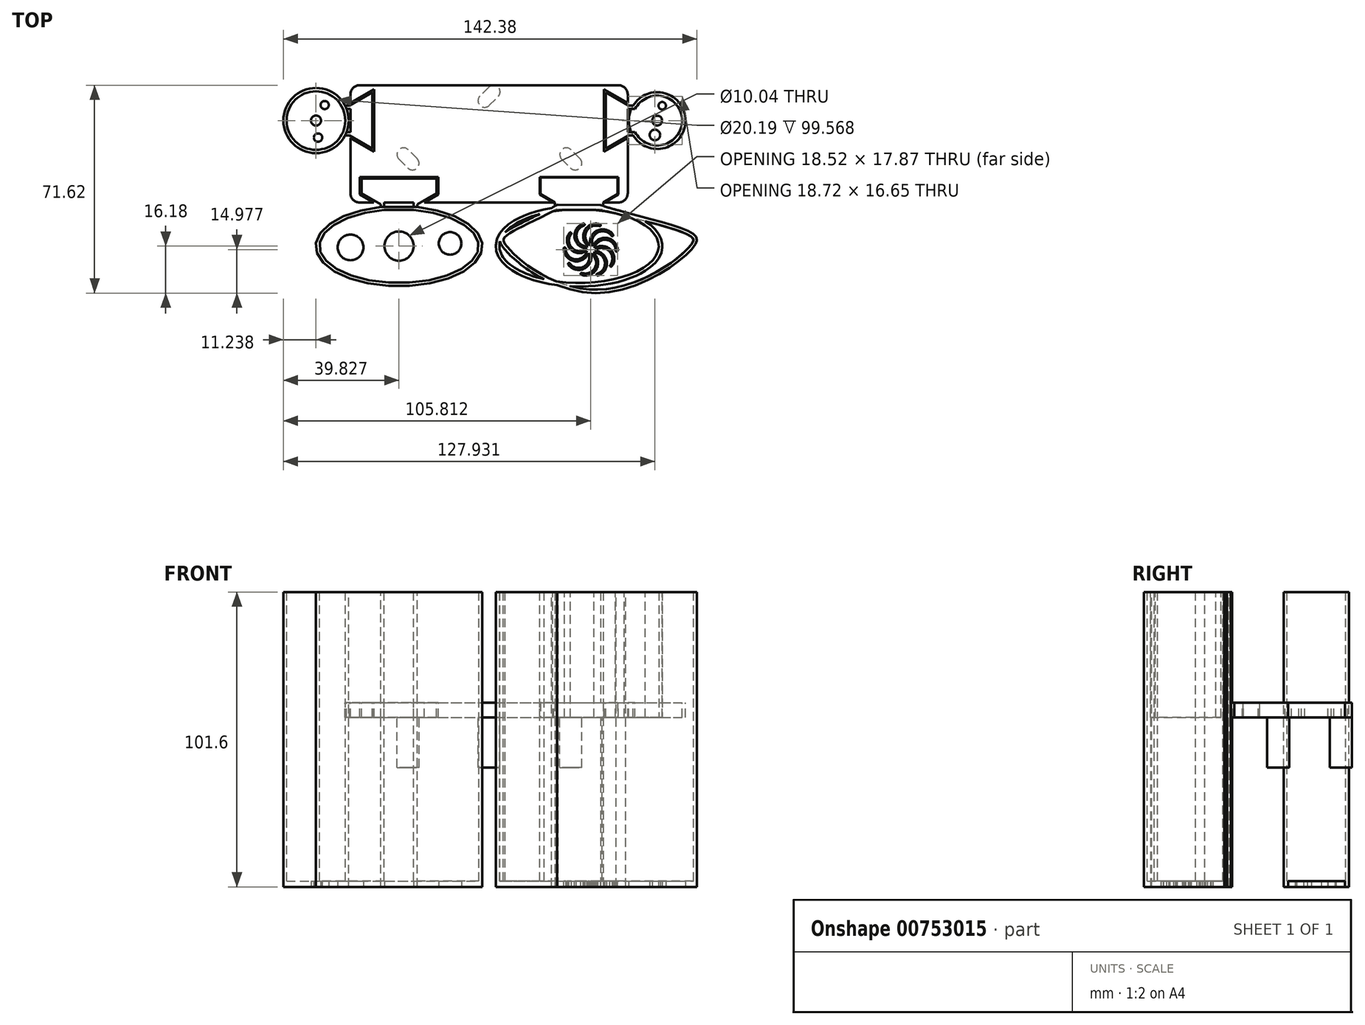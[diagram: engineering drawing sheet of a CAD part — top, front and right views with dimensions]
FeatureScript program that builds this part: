
annotation { "Feature Type Name" : "Feature", "Feature Type Description" : "" }
export const myFeature = defineFeature(function(context is Context, id is Id, definition is map)
    precondition{}
    {
        {
            var Q0;
            Q0=qCreatedBy(makeId("Top.planeOp"),FACE);
            var sketch = newSketch(context, id + "F0", { "sketchPlane" : qUnion([Q0])});
            skLineSegment(sketch, "E0.bottom", {"start": v(-47.75, 97.16) * mm, "end": v(47.75, 97.16) * mm, "construction": true});
            skLineSegment(sketch, "E0.top", {"start": v(-44.58, 0) * mm, "end": v(44.58, 0) * mm});
            skLineSegment(sketch, "E0.left", {"start": v(-47.75, 37.25) * mm, "end": v(-47.75, 3.17) * mm});
            skLineSegment(sketch, "E0.right", {"start": v(47.75, 37.25) * mm, "end": v(47.75, 3.18) * mm});
            skLineSegment(sketch, "E1", {"start": v(25.02, 14.93) * mm, "end": v(28.07, 11.88) * mm});
            skArc(sketch, "E2", {"start": v(28.07, 11.88) * mm, "mid": v(31.3, 11.88) * mm, "end": v(31.3, 15.11) * mm});
            skLineSegment(sketch, "E3", {"start": v(31.3, 15.11) * mm, "end": v(28.25, 18.16) * mm});
            skArc(sketch, "E4", {"start": v(28.25, 18.16) * mm, "mid": v(25.02, 18.16) * mm, "end": v(25.02, 14.93) * mm});
            skLineSegment(sketch, "E5", {"start": v(23, 15.51) * mm, "end": v(28.65, 9.86) * mm, "construction": true});
            skArc(sketch, "E6", {"start": v(28.65, 9.86) * mm, "mid": v(33.32, 9.86) * mm, "end": v(33.32, 14.53) * mm, "construction": true});
            skLineSegment(sketch, "E7", {"start": v(33.32, 14.53) * mm, "end": v(27.67, 20.18) * mm, "construction": true});
            skArc(sketch, "E8", {"start": v(27.67, 20.18) * mm, "mid": v(23, 20.18) * mm, "end": v(23, 15.51) * mm, "construction": true});
            skLineSegment(sketch, "E9", {"start": v(-31.04, 14.93) * mm, "end": v(-27.99, 11.88) * mm});
            skArc(sketch, "E10", {"start": v(-27.99, 11.88) * mm, "mid": v(-24.76, 11.88) * mm, "end": v(-24.76, 15.11) * mm});
            skLineSegment(sketch, "E11", {"start": v(-24.76, 15.11) * mm, "end": v(-27.8, 18.16) * mm});
            skArc(sketch, "E12", {"start": v(-27.8, 18.16) * mm, "mid": v(-31.04, 18.16) * mm, "end": v(-31.04, 14.93) * mm});
            skLineSegment(sketch, "E13", {"start": v(0.09, 33.47) * mm, "end": v(3.14, 36.52) * mm});
            skArc(sketch, "E14", {"start": v(3.14, 36.52) * mm, "mid": v(3.14, 39.75) * mm, "end": v(-0.09, 39.75) * mm});
            skLineSegment(sketch, "E15", {"start": v(-0.09, 39.75) * mm, "end": v(-3.14, 36.7) * mm});
            skArc(sketch, "E16", {"start": v(-3.14, 36.7) * mm, "mid": v(-3.14, 33.47) * mm, "end": v(0.09, 33.47) * mm});
            skLineSegment(sketch, "E17", {"start": v(25.33, 17.85) * mm, "end": v(30.99, 12.2) * mm, "construction": true});
            skLineSegment(sketch, "E18", {"start": v(26.63, 16.55) * mm, "end": v(29.69, 13.5) * mm, "construction": true});
            skPoint(sketch, "E19", {"position": v(28.16, 15.02) * mm});
            skLineSegment(sketch, "E20", {"start": v(-1.53, 35.08) * mm, "end": v(1.53, 38.14) * mm, "construction": true});
            skLineSegment(sketch, "E21", {"start": v(-29.43, 16.55) * mm, "end": v(-26.37, 13.5) * mm, "construction": true});
            skPoint(sketch, "E22", {"position": v(0, 36.61) * mm});
            skLineSegment(sketch, "E23", {"start": v(26.48, 8.9) * mm, "end": v(34.3, 8.89) * mm, "construction": true});
            skLineSegment(sketch, "E24", {"start": v(34.3, 8.89) * mm, "end": v(34.3, 17.52) * mm, "construction": true});
            skLineSegment(sketch, "E25", {"start": v(-44.58, 40.42) * mm, "end": v(44.58, 40.42) * mm});
            skPoint(sketch, "E26.visualSharp", {"position": v(-47.75, 0) * mm});
            skArc(sketch, "E26.filletArc", {"start": v(-47.75, 3.17) * mm, "mid": v(-46.82, 0.93) * mm, "end": v(-44.58, 0) * mm});
            skPoint(sketch, "E27.visualSharp", {"position": v(47.75, 0) * mm});
            skArc(sketch, "E27.filletArc", {"start": v(44.58, 0) * mm, "mid": v(46.82, 0.93) * mm, "end": v(47.75, 3.18) * mm});
            skArc(sketch, "E28.filletArc", {"start": v(47.75, 37.25) * mm, "mid": v(46.82, 39.5) * mm, "end": v(44.58, 40.42) * mm});
            skArc(sketch, "E29.filletArc", {"start": v(-44.58, 40.42) * mm, "mid": v(-46.82, 39.5) * mm, "end": v(-47.75, 37.25) * mm});
            skSolve(sketch);
        }
        {
            var Q0;
            Q0=makeQuery(id+"F0.imprint","IMPRINT",FACE,{"disambiguationData":[TD([[makeQuery(id+"F0.imprint","IMPRINT",EDGE,{"derivedFrom":sQuery(id+"F0.wireOp",EDGE,"E0.top")}),1.0]])]});
            var Q1;
            Q1=makeQuery(id+"F0.imprint","IMPRINT",FACE,{"disambiguationData":[TD([[makeQuery(id+"F0.imprint","IMPRINT",EDGE,{"derivedFrom":sQuery(id+"F0.wireOp",EDGE,"E9")}),1.0]])]});
            var Q2;
            {var subQ3=sQuery(id+"F0.wireOp",EDGE,"E13");Q2=makeQuery(id+"F0.imprint","IMPRINT",FACE,{"disambiguationData":[TD([[makeQuery(id+"F0.imprint","IMPRINT",EDGE,{"derivedFrom":subQ3}),1.0]])]});}
            var Q3;
            Q3=makeQuery(id+"F0.imprint","IMPRINT",FACE,{"disambiguationData":[TD([[makeQuery(id+"F0.imprint","IMPRINT",EDGE,{"derivedFrom":sQuery(id+"F0.wireOp",EDGE,"E1")}),1.0]])]});
            extrude(context, id + "F1", {"entities" : qUnion([Q0, Q1, Q2, Q3]), "depth" : 5.08 * mm, "offsetDistance" : 25.4 * mm});
        }
        {
            var Q0;
            Q0=makeQuery(id+"F0.imprint","IMPRINT",FACE,{"disambiguationData":[TD([[makeQuery(id+"F0.imprint","IMPRINT",EDGE,{"derivedFrom":sQuery(id+"F0.wireOp",EDGE,"E1")}),1.0]])]});
            var Q1;
            {var subQ3=sQuery(id+"F0.wireOp",EDGE,"E13");Q1=makeQuery(id+"F0.imprint","IMPRINT",FACE,{"disambiguationData":[TD([[makeQuery(id+"F0.imprint","IMPRINT",EDGE,{"derivedFrom":subQ3}),1.0]])]});}
            var Q2;
            Q2=makeQuery(id+"F0.imprint","IMPRINT",FACE,{"disambiguationData":[TD([[makeQuery(id+"F0.imprint","IMPRINT",EDGE,{"derivedFrom":sQuery(id+"F0.wireOp",EDGE,"E9")}),1.0]])]});
            var Q3;
            Q3=sQuery(id+"F0.wireOp",EDGE,"E2");
            var Q4;
            Q4=sQuery(id+"F0.wireOp",EDGE,"E3");
            var Q5;
            Q5=sQuery(id+"F0.wireOp",EDGE,"E4");
            var Q6;
            Q6=sQuery(id+"F0.wireOp",EDGE,"E1");
            extrude(context, id + "F2", {"entities" : qUnion([Q0, Q1, Q2]), "operationType" : NewBodyOperationType.ADD, "surfaceEntities" : qUnion([Q3, Q4, Q5, Q6]), "oppositeDirection" : true, "depth" : 17.27 * mm, "offsetDistance" : 25.4 * mm});
        }
        {
            var Q0;
            Q0=makeQuery(id+"F1.opExtrude","CAP_FACE",FACE,{"disambiguationData":[OSD([sQuery(id+"F0.wireOp",EDGE,"E0.top"),sQuery(id+"F0.wireOp",EDGE,"E0.left"),sQuery(id+"F0.wireOp",EDGE,"E0.right"),sQuery(id+"F0.wireOp",EDGE,"E25"),sQuery(id+"F0.wireOp",EDGE,"E26.filletArc"),sQuery(id+"F0.wireOp",EDGE,"E27.filletArc"),sQuery(id+"F0.wireOp",EDGE,"E28.filletArc"),sQuery(id+"F0.wireOp",EDGE,"E29.filletArc")])],"isStart":false});
            var sketch = newSketch(context, id + "F3", { "sketchPlane" : qUnion([Q0])});
            skLineSegment(sketch, "E30", {"start": v(47.75, 32.19) * mm, "end": v(41.4, 35.85) * mm});
            skLineSegment(sketch, "E31", {"start": v(41.4, 35.85) * mm, "end": v(41.4, 20.61) * mm});
            skLineSegment(sketch, "E32", {"start": v(41.4, 20.61) * mm, "end": v(47.75, 24.28) * mm});
            skLineSegment(sketch, "E33", {"start": v(47.75, 32.19) * mm, "end": v(47.75, 24.28) * mm});
            skLineSegment(sketch, "E34", {"start": v(47.75, 32.19) * mm, "end": v(50.3, 32.19) * mm});
            skArc(sketch, "E35", {"start": v(50.3, 24.28) * mm, "mid": v(66.47, 28.23) * mm, "end": v(50.3, 32.19) * mm});
            skLineSegment(sketch, "E36", {"start": v(50.3, 24.28) * mm, "end": v(47.75, 24.28) * mm});
            skLineSegment(sketch, "E37", {"start": v(41.4, 28.23) * mm, "end": v(57.9, 28.23) * mm, "construction": true});
            skLineSegment(sketch, "E38", {"start": v(50.3, 32.19) * mm, "end": v(50.3, 24.28) * mm, "construction": true});
            skPoint(sketch, "E39.positionSnap0", {"position": v(50.3, 28.23) * mm});
            skEllipticalArc(sketch, "E40", {});
            skLineSegment(sketch, "E41", {"start": v(31, -15.02) * mm, "end": v(58.42, -15.02) * mm, "construction": true});
            skLineSegment(sketch, "E42", {"start": v(25.91, 0) * mm, "end": v(19.31, 3.8) * mm});
            skLineSegment(sketch, "E43", {"start": v(19.31, 3.81) * mm, "end": v(19.31, 6.99) * mm});
            skLineSegment(sketch, "E44", {"start": v(19.31, 6.99) * mm, "end": v(42.67, 6.99) * mm});
            skLineSegment(sketch, "E45", {"start": v(42.67, 6.99) * mm, "end": v(42.67, 3.81) * mm});
            skLineSegment(sketch, "E46", {"start": v(42.67, 3.8) * mm, "end": v(36.07, 0) * mm});
            skLineSegment(sketch, "E47", {"start": v(36.07, 0) * mm, "end": v(25.91, 0) * mm});
            skLineSegment(sketch, "E48", {"start": v(31, 0) * mm, "end": v(31, 6.99) * mm, "construction": true});
            skLineSegment(sketch, "E49", {"start": v(25.91, 0) * mm, "end": v(25.91, -2.54) * mm});
            skLineSegment(sketch, "E50", {"start": v(36.07, 0) * mm, "end": v(36.07, -2.54) * mm});
            skFitSpline(sketch, "E51.0", {"points": [v(59.52, -16.54) * mm, v(59.68, -15.02) * mm, v(59.52, -13.5) * mm, v(59.04, -12.04) * mm, v(58.29, -10.65) * mm, v(57.27, -9.35) * mm, v(56.02, -8.12) * mm, v(54.54, -6.97) * mm, v(53.12, -6.09) * mm, v(51.88, -5.42) * mm, v(50.9, -4.95) * mm, v(49.87, -4.5) * mm, v(48.45, -3.93) * mm, v(46.59, -3.29) * mm, v(44.22, -2.63) * mm, v(41.73, -2.09) * mm, v(39.15, -1.66) * mm, v(36.5, -1.35) * mm, v(34.22, -1.2) * mm, v(32.38, -1.13) * mm, v(31, -1.12) * mm, v(29.6, -1.13) * mm, v(27.77, -1.2) * mm, v(25.5, -1.35) * mm, v(22.83, -1.66) * mm, v(20.25, -2.09) * mm, v(17.77, -2.63) * mm, v(15.4, -3.29) * mm, v(13.53, -3.93) * mm, v(12.11, -4.5) * mm, v(11.08, -4.95) * mm, v(10.1, -5.42) * mm, v(8.86, -6.09) * mm, v(7.45, -6.97) * mm, v(5.97, -8.12) * mm, v(4.71, -9.35) * mm, v(3.7, -10.65) * mm, v(2.94, -12.04) * mm, v(2.47, -13.5) * mm, v(2.3, -15.02) * mm, v(2.47, -16.54) * mm, v(2.94, -18) * mm, v(3.7, -19.39) * mm, v(4.71, -20.7) * mm, v(5.97, -21.92) * mm, v(7.45, -23.07) * mm, v(8.86, -23.95) * mm, v(10.1, -24.62) * mm, v(11.08, -25.1) * mm, v(12.11, -25.55) * mm, v(13.53, -26.11) * mm, v(15.4, -26.75) * mm, v(17.77, -27.4) * mm, v(20.25, -27.95) * mm, v(22.83, -28.38) * mm, v(25.5, -28.69) * mm, v(27.77, -28.85) * mm, v(29.6, -28.9) * mm, v(31, -28.93) * mm, v(32.38, -28.9) * mm, v(34.22, -28.85) * mm, v(36.5, -28.69) * mm, v(39.15, -28.38) * mm, v(41.73, -27.95) * mm, v(44.22, -27.4) * mm, v(46.59, -26.75) * mm, v(48.45, -26.11) * mm, v(49.87, -25.55) * mm, v(50.9, -25.1) * mm, v(51.88, -24.62) * mm, v(53.12, -23.95) * mm, v(54.54, -23.07) * mm, v(56.02, -21.92) * mm, v(57.27, -20.7) * mm, v(58.29, -19.39) * mm, v(59.04, -18) * mm, v(59.52, -16.54) * mm, v(59.68, -15.02) * mm, v(59.52, -13.5) * mm]});
            skLineSegment(sketch, "E51.1", {"start": v(18.11, 3.12) * mm, "end": v(18.11, 8.19) * mm});
            skLineSegment(sketch, "E51.2", {"start": v(18.11, 8.19) * mm, "end": v(43.87, 8.19) * mm});
            skLineSegment(sketch, "E51.3", {"start": v(43.87, 8.19) * mm, "end": v(43.87, 3.12) * mm});
            skLineSegment(sketch, "E52", {"start": v(24.71, -0.7) * mm, "end": v(18.11, 3.12) * mm});
            skLineSegment(sketch, "E53", {"start": v(18.11, -2.57) * mm, "end": v(24.71, -1.58) * mm});
            skLineSegment(sketch, "E54.MirrorCS", {"start": v(37.27, -0.7) * mm, "end": v(43.87, 3.12) * mm});
            skLineSegment(sketch, "E55.MirrorCS", {"start": v(43.87, -2.57) * mm, "end": v(37.27, -1.58) * mm});
            skLineSegment(sketch, "E56.MirrorCS", {"start": v(37.27, -1.58) * mm, "end": v(37.27, -0.7) * mm});
            skLineSegment(sketch, "E57.0", {"start": v(39.67, 0) * mm, "end": v(44.47, 2.77) * mm});
            skLineSegment(sketch, "E57.1", {"start": v(22.31, 0) * mm, "end": v(17.51, 2.77) * mm});
            skLineSegment(sketch, "E57.2", {"start": v(17.51, 2.77) * mm, "end": v(17.51, 8.78) * mm});
            skLineSegment(sketch, "E57.3", {"start": v(17.51, 8.78) * mm, "end": v(44.47, 8.78) * mm});
            skLineSegment(sketch, "E57.4", {"start": v(44.47, 8.78) * mm, "end": v(44.47, 2.77) * mm});
            skLineSegment(sketch, "E58", {"start": v(22.31, 0) * mm, "end": v(39.67, 0) * mm});
            skLineSegment(sketch, "E59.0", {"start": v(49.6, 23.08) * mm, "end": v(48.07, 23.08) * mm});
            skLineSegment(sketch, "E59.1", {"start": v(48.07, 33.39) * mm, "end": v(49.6, 33.39) * mm});
            skLineSegment(sketch, "E59.2", {"start": v(48.07, 33.39) * mm, "end": v(40.2, 37.93) * mm});
            skLineSegment(sketch, "E59.3", {"start": v(40.2, 37.93) * mm, "end": v(40.2, 18.53) * mm});
            skLineSegment(sketch, "E59.4", {"start": v(40.2, 18.53) * mm, "end": v(48.07, 23.08) * mm});
            skArc(sketch, "E60.0", {"start": v(49.6, 23.08) * mm, "mid": v(67.67, 28.23) * mm, "end": v(49.6, 33.39) * mm});
            skLineSegment(sketch, "E61.0", {"start": v(39.6, 17.5) * mm, "end": v(47.75, 22.2) * mm});
            skLineSegment(sketch, "E61.1", {"start": v(39.6, 38.97) * mm, "end": v(39.6, 17.5) * mm});
            skLineSegment(sketch, "E61.2", {"start": v(47.75, 34.26) * mm, "end": v(39.6, 38.97) * mm});
            skLineSegment(sketch, "E62", {"start": v(47.75, 34.26) * mm, "end": v(47.75, 22.2) * mm});
            skLineSegment(sketch, "E63.MirrorCS", {"start": v(-39.6, 38.97) * mm, "end": v(-39.6, 17.5) * mm});
            skLineSegment(sketch, "E64.MirrorCS", {"start": v(-40.2, 37.93) * mm, "end": v(-40.2, 18.53) * mm});
            skLineSegment(sketch, "E65.MirrorCS", {"start": v(-47.75, 34.26) * mm, "end": v(-39.6, 38.97) * mm});
            skLineSegment(sketch, "E66.MirrorCS", {"start": v(-48.07, 33.39) * mm, "end": v(-40.2, 37.93) * mm});
            skLineSegment(sketch, "E67.MirrorCS", {"start": v(-41.4, 35.85) * mm, "end": v(-41.4, 20.61) * mm});
            skLineSegment(sketch, "E68.MirrorCS", {"start": v(-47.75, 32.19) * mm, "end": v(-41.4, 35.85) * mm});
            skLineSegment(sketch, "E69.MirrorCS", {"start": v(-41.4, 20.61) * mm, "end": v(-47.75, 24.28) * mm});
            skLineSegment(sketch, "E70.MirrorCS", {"start": v(-40.2, 18.53) * mm, "end": v(-48.07, 23.08) * mm});
            skLineSegment(sketch, "E71.MirrorCS", {"start": v(-39.6, 17.5) * mm, "end": v(-47.75, 22.2) * mm});
            skLineSegment(sketch, "E72.MirrorCS", {"start": v(-47.75, 34.26) * mm, "end": v(-47.75, 22.2) * mm});
            skLineSegment(sketch, "E73.MirrorCS", {"start": v(-50.3, 24.28) * mm, "end": v(-47.75, 24.28) * mm});
            skLineSegment(sketch, "E74.MirrorCS", {"start": v(-49.6, 23.08) * mm, "end": v(-48.07, 23.08) * mm});
            skArc(sketch, "E75.MirrorCS", {"start": v(-49.6, 23.08) * mm, "mid": v(-70.82, 28.23) * mm, "end": v(-49.6, 33.39) * mm});
            skArc(sketch, "E76.MirrorCS", {"start": v(-50.3, 24.28) * mm, "mid": v(-69.68, 28.23) * mm, "end": v(-50.3, 32.19) * mm});
            skLineSegment(sketch, "E77.MirrorCS", {"start": v(-47.75, 32.19) * mm, "end": v(-50.3, 32.19) * mm});
            skLineSegment(sketch, "E78.MirrorCS", {"start": v(-48.07, 33.39) * mm, "end": v(-49.6, 33.39) * mm});
            skLineSegment(sketch, "E79.MirrorCS", {"start": v(-17.51, 8.78) * mm, "end": v(-44.47, 8.78) * mm});
            skLineSegment(sketch, "E80.MirrorCS", {"start": v(-18.11, 8.19) * mm, "end": v(-43.87, 8.19) * mm});
            skLineSegment(sketch, "E81.MirrorCS", {"start": v(-19.31, 6.99) * mm, "end": v(-42.67, 6.99) * mm});
            skLineSegment(sketch, "E82.MirrorCS", {"start": v(-19.31, 3.81) * mm, "end": v(-19.31, 6.99) * mm});
            skLineSegment(sketch, "E83.MirrorCS", {"start": v(-18.11, 3.12) * mm, "end": v(-18.11, 8.19) * mm});
            skLineSegment(sketch, "E84.MirrorCS", {"start": v(-17.51, 2.77) * mm, "end": v(-17.51, 8.78) * mm});
            skLineSegment(sketch, "E85.MirrorCS", {"start": v(-22.31, 0) * mm, "end": v(-17.51, 2.77) * mm});
            skLineSegment(sketch, "E86.MirrorCS", {"start": v(-24.71, -0.7) * mm, "end": v(-18.11, 3.12) * mm});
            skLineSegment(sketch, "E87.MirrorCS", {"start": v(-25.91, 0) * mm, "end": v(-19.31, 3.8) * mm});
            skLineSegment(sketch, "E88.MirrorCS", {"start": v(-25.91, 0) * mm, "end": v(-25.91, -2.54) * mm});
            skLineSegment(sketch, "E89.MirrorCS", {"start": v(-24.71, -1.58) * mm, "end": v(-24.71, -0.7) * mm});
            skLineSegment(sketch, "E90.MirrorCS", {"start": v(-22.31, 0) * mm, "end": v(-39.67, 0) * mm});
            skEllipticalArc(sketch, "E91.MirrorCS", {});
            skLineSegment(sketch, "E92.MirrorCS", {"start": v(-36.07, 0) * mm, "end": v(-36.07, -2.54) * mm});
            skLineSegment(sketch, "E93.MirrorCS", {"start": v(-37.27, -1.58) * mm, "end": v(-37.27, -0.7) * mm});
            skLineSegment(sketch, "E94.MirrorCS", {"start": v(-37.27, -0.7) * mm, "end": v(-43.87, 3.12) * mm});
            skLineSegment(sketch, "E95.MirrorCS", {"start": v(-42.67, 3.8) * mm, "end": v(-36.07, 0) * mm});
            skLineSegment(sketch, "E96.MirrorCS", {"start": v(-39.67, 0) * mm, "end": v(-44.47, 2.77) * mm});
            skLineSegment(sketch, "E97.MirrorCS", {"start": v(-42.67, 6.99) * mm, "end": v(-42.67, 3.81) * mm});
            skLineSegment(sketch, "E98.MirrorCS", {"start": v(-43.87, 8.19) * mm, "end": v(-43.87, 3.12) * mm});
            skLineSegment(sketch, "E99.MirrorCS", {"start": v(-44.47, 8.78) * mm, "end": v(-44.47, 2.77) * mm});
            skEllipticalArc(sketch, "E100", {});
            skLineSegment(sketch, "E101", {"start": v(24.71, -1.58) * mm, "end": v(24.71, -0.7) * mm});
            const initialGuessF3  = {"E40": [0.030992886423162575, -0.015020336248152173, 1, 0, 0.027432, 0.0127, 1.7570566303714528, 1.3845360232183404], "E91.MirrorCS": [-0.030992886423162575, -0.015020336248152173, -1, 0, 0.027432, 0.0127, 4.898649283961246, 4.526128676808133], "E100": [-0.030992886423162575, -0.015020336248152173, -1, 0, 0.02867695838303173, 0.013772825850373925, 4.933169380153746, 4.491608580615633]};
            skSetInitialGuess(sketch, initialGuessF3);
            skSolve(sketch);
        }
        {
            var Q0;
            Q0=makeQuery(id+"F3.imprint","IMPRINT",FACE,{"disambiguationData":[TD([[makeQuery(id+"F3.imprint","IMPRINT",EDGE,{"derivedFrom":sQuery(id+"F3.wireOp",EDGE,"E81.MirrorCS")}),1.0]])]});
            var Q1;
            Q1=makeQuery(id+"F3.imprint","IMPRINT",FACE,{"disambiguationData":[TD([[makeQuery(id+"F3.imprint","IMPRINT",EDGE,{"derivedFrom":sQuery(id+"F3.wireOp",EDGE,"E80.MirrorCS")}),1.0]])]});
            var Q2;
            Q2=makeQuery(id+"F3.imprint","IMPRINT",FACE,{"disambiguationData":[TD([[makeQuery(id+"F3.imprint","IMPRINT",EDGE,{"derivedFrom":sQuery(id+"F3.wireOp",EDGE,"E79.MirrorCS")}),1.0]])]});
            var Q3;
            Q3=makeQuery(id+"F3.imprint","IMPRINT",FACE,{"disambiguationData":[TD([[makeQuery(id+"F3.imprint","IMPRINT",EDGE,{"derivedFrom":sQuery(id+"F3.wireOp",EDGE,"E63.MirrorCS")}),-1.0]])]});
            var Q4;
            {var subQ1=sQuery(id+"F3.wireOp",EDGE,"E64.MirrorCS");Q4=makeQuery(id+"F3.imprint","IMPRINT",FACE,{"disambiguationData":[TD([[makeQuery(id+"F3.imprint","IMPRINT",EDGE,{"derivedFrom":subQ1}),-1.0]])]});}
            var Q5;
            Q5=makeQuery(id+"F3.imprint","IMPRINT",FACE,{"disambiguationData":[TD([[makeQuery(id+"F3.imprint","IMPRINT",EDGE,{"derivedFrom":sQuery(id+"F3.wireOp",EDGE,"E67.MirrorCS")}),-1.0]])]});
            var Q6;
            {var subQ1=sQuery(id+"F3.wireOp",EDGE,"E42");Q6=makeQuery(id+"F3.imprint","IMPRINT",FACE,{"disambiguationData":[TD([[makeQuery(id+"F3.imprint","IMPRINT",EDGE,{"derivedFrom":subQ1}),-1.0]])]});}
            var Q7;
            {var subQ6=sQuery(id+"F3.wireOp",EDGE,"E42");Q7=makeQuery(id+"F3.imprint","IMPRINT",FACE,{"disambiguationData":[TD([[makeQuery(id+"F3.imprint","IMPRINT",EDGE,{"derivedFrom":subQ6}),1.0]])]});}
            var Q8;
            {var subQ6=sQuery(id+"F3.wireOp",EDGE,"E51.1");Q8=makeQuery(id+"F3.imprint","IMPRINT",FACE,{"disambiguationData":[TD([[makeQuery(id+"F3.imprint","IMPRINT",EDGE,{"derivedFrom":subQ6}),1.0]])]});}
            var Q9;
            {var subQ0=sQuery(id+"F3.wireOp",EDGE,"E30");Q9=makeQuery(id+"F3.imprint","IMPRINT",FACE,{"disambiguationData":[TD([[makeQuery(id+"F3.imprint","IMPRINT",EDGE,{"derivedFrom":subQ0}),1.0]])]});}
            var Q10;
            {var subQ7=sQuery(id+"F3.wireOp",EDGE,"E30");Q10=makeQuery(id+"F3.imprint","IMPRINT",FACE,{"disambiguationData":[TD([[makeQuery(id+"F3.imprint","IMPRINT",EDGE,{"derivedFrom":subQ7}),-1.0]])]});}
            var Q11;
            {var subQ1=sQuery(id+"F3.wireOp",EDGE,"E59.3");Q11=makeQuery(id+"F3.imprint","IMPRINT",FACE,{"disambiguationData":[TD([[makeQuery(id+"F3.imprint","IMPRINT",EDGE,{"derivedFrom":subQ1}),-1.0]])]});}
            extrude(context, id + "F4", {"entities" : qUnion([Q0, Q1, Q2, Q3, Q4, Q5, Q6, Q7, Q8, Q9, Q10, Q11]), "operationType" : NewBodyOperationType.REMOVE, "oppositeDirection" : true, "depth" : 25.4 * mm, "offsetDistance" : 25.4 * mm});
        }
        {
            var Q0;
            {var subQ1=sQuery(id+"F3.wireOp",EDGE,"E64.MirrorCS");Q0=makeQuery(id+"F3.imprint","IMPRINT",FACE,{"disambiguationData":[TD([[makeQuery(id+"F3.imprint","IMPRINT",EDGE,{"derivedFrom":subQ1}),-1.0]])]});}
            var Q1;
            {var subQ4=sQuery(id+"F3.wireOp",EDGE,"E73.MirrorCS");Q1=makeQuery(id+"F3.imprint","IMPRINT",FACE,{"disambiguationData":[TD([[makeQuery(id+"F3.imprint","IMPRINT",EDGE,{"derivedFrom":subQ4}),-1.0]])]});}
            var Q2;
            {var subQ5=sQuery(id+"F3.wireOp",EDGE,"E88.MirrorCS");Q2=makeQuery(id+"F3.imprint","IMPRINT",FACE,{"disambiguationData":[TD([[makeQuery(id+"F3.imprint","IMPRINT",EDGE,{"derivedFrom":subQ5}),1.0]])]});}
            var Q3;
            Q3=makeQuery(id+"F3.imprint","IMPRINT",FACE,{"disambiguationData":[TD([[makeQuery(id+"F3.imprint","IMPRINT",EDGE,{"derivedFrom":sQuery(id+"F3.wireOp",EDGE,"E80.MirrorCS")}),1.0]])]});
            var Q4;
            {var subQ6=sQuery(id+"F3.wireOp",EDGE,"E42");Q4=makeQuery(id+"F3.imprint","IMPRINT",FACE,{"disambiguationData":[TD([[makeQuery(id+"F3.imprint","IMPRINT",EDGE,{"derivedFrom":subQ6}),1.0]])]});}
            var Q5;
            Q5=makeQuery(id+"F3.imprint","IMPRINT",FACE,{"disambiguationData":[TD([[makeQuery(id+"F3.imprint","IMPRINT",EDGE,{"derivedFrom":sQuery(id+"F3.wireOp",EDGE,"E40")}),-1.0]])]});
            var Q6;
            {var subQ7=sQuery(id+"F3.wireOp",EDGE,"E30");Q6=makeQuery(id+"F3.imprint","IMPRINT",FACE,{"disambiguationData":[TD([[makeQuery(id+"F3.imprint","IMPRINT",EDGE,{"derivedFrom":subQ7}),-1.0]])]});}
            var Q7;
            {var subQ8=sQuery(id+"F3.wireOp",EDGE,"E34");Q7=makeQuery(id+"F3.imprint","IMPRINT",FACE,{"disambiguationData":[TD([[makeQuery(id+"F3.imprint","IMPRINT",EDGE,{"derivedFrom":subQ8}),1.0]])]});}
            var Q8;
            Q8=makeQuery(id+"F3.imprint","IMPRINT",FACE,{"disambiguationData":[TD([[makeQuery(id+"F3.imprint","IMPRINT",EDGE,{"derivedFrom":sQuery(id+"F3.wireOp",EDGE,"E81.MirrorCS")}),1.0]])]});
            var Q9;
            Q9=makeQuery(id+"F3.imprint","IMPRINT",FACE,{"disambiguationData":[TD([[makeQuery(id+"F3.imprint","IMPRINT",EDGE,{"derivedFrom":sQuery(id+"F3.wireOp",EDGE,"E67.MirrorCS")}),-1.0]])]});
            var Q10;
            {var subQ1=sQuery(id+"F3.wireOp",EDGE,"E42");Q10=makeQuery(id+"F3.imprint","IMPRINT",FACE,{"disambiguationData":[TD([[makeQuery(id+"F3.imprint","IMPRINT",EDGE,{"derivedFrom":subQ1}),-1.0]])]});}
            var Q11;
            {var subQ0=sQuery(id+"F3.wireOp",EDGE,"E30");Q11=makeQuery(id+"F3.imprint","IMPRINT",FACE,{"disambiguationData":[TD([[makeQuery(id+"F3.imprint","IMPRINT",EDGE,{"derivedFrom":subQ0}),1.0]])]});}
            extrude(context, id + "F5", {"entities" : qUnion([Q0, Q1, Q2, Q3, Q4, Q5, Q6, Q7, Q8, Q9, Q10, Q11]), "oppositeDirection" : true, "depth" : 5.08 * mm, "offsetDistance" : 25.4 * mm});
        }
        {
            var Q0;
            Q0=makeQuery(id+"F5.opExtrude","CAP_FACE",FACE,{"disambiguationData":[OSD([sQuery(id+"F3.wireOp",EDGE,"E80.MirrorCS"),sQuery(id+"F3.wireOp",EDGE,"E81.MirrorCS"),sQuery(id+"F3.wireOp",EDGE,"E82.MirrorCS"),sQuery(id+"F3.wireOp",EDGE,"E83.MirrorCS"),sQuery(id+"F3.wireOp",EDGE,"E86.MirrorCS"),sQuery(id+"F3.wireOp",EDGE,"E87.MirrorCS"),sQuery(id+"F3.wireOp",EDGE,"E88.MirrorCS"),sQuery(id+"F3.wireOp",EDGE,"E89.MirrorCS"),sQuery(id+"F3.wireOp",EDGE,"E91.MirrorCS"),sQuery(id+"F3.wireOp",EDGE,"E92.MirrorCS"),sQuery(id+"F3.wireOp",EDGE,"E93.MirrorCS"),sQuery(id+"F3.wireOp",EDGE,"E94.MirrorCS"),sQuery(id+"F3.wireOp",EDGE,"E95.MirrorCS"),sQuery(id+"F3.wireOp",EDGE,"E97.MirrorCS"),sQuery(id+"F3.wireOp",EDGE,"E98.MirrorCS"),sQuery(id+"F3.wireOp",EDGE,"E100")])],"isStart":false});
            var sketch = newSketch(context, id + "F6", { "sketchPlane" : qUnion([Q0])});
            skEllipticalArc(sketch, "E102.0", {});
            skEllipticalArc(sketch, "E103.0", {});
            skArc(sketch, "E103.1", {"start": v(-49.6, -23.08) * mm, "mid": v(-70.82, -28.23) * mm, "end": v(-49.6, -33.39) * mm});
            skArc(sketch, "E103.2", {"start": v(-50.3, -24.28) * mm, "mid": v(-69.68, -28.23) * mm, "end": v(-50.3, -32.19) * mm});
            skEllipticalArc(sketch, "E103.3", {});
            skFitSpline(sketch, "E103.4", {"points": [v(59.62, 15.02) * mm, v(59.62, 14.51) * mm, v(59.52, 13.5) * mm, v(59.04, 12.04) * mm, v(58.29, 10.65) * mm, v(57.27, 9.35) * mm, v(56.02, 8.12) * mm, v(54.54, 6.97) * mm, v(53.12, 6.09) * mm, v(51.88, 5.42) * mm, v(50.9, 4.95) * mm, v(49.87, 4.5) * mm, v(48.45, 3.93) * mm, v(46.59, 3.29) * mm, v(44.22, 2.63) * mm, v(41.73, 2.09) * mm, v(39.15, 1.66) * mm, v(36.5, 1.35) * mm, v(34.22, 1.2) * mm, v(32.38, 1.13) * mm, v(31, 1.12) * mm, v(29.6, 1.13) * mm, v(27.77, 1.2) * mm, v(25.5, 1.35) * mm, v(22.83, 1.66) * mm, v(20.25, 2.09) * mm, v(17.77, 2.63) * mm, v(15.4, 3.29) * mm, v(13.53, 3.93) * mm, v(12.11, 4.5) * mm, v(11.08, 4.95) * mm, v(10.1, 5.42) * mm, v(8.86, 6.09) * mm, v(7.45, 6.97) * mm, v(5.97, 8.12) * mm, v(4.71, 9.35) * mm, v(3.7, 10.65) * mm, v(2.94, 12.04) * mm, v(2.47, 13.5) * mm, v(2.3, 15.02) * mm, v(2.47, 16.54) * mm, v(2.94, 18) * mm, v(3.7, 19.39) * mm, v(4.71, 20.7) * mm, v(5.97, 21.92) * mm, v(7.45, 23.07) * mm, v(8.86, 23.95) * mm, v(10.1, 24.62) * mm, v(11.08, 25.1) * mm, v(12.11, 25.55) * mm, v(13.53, 26.11) * mm, v(15.4, 26.75) * mm, v(17.77, 27.4) * mm, v(20.25, 27.95) * mm, v(22.83, 28.38) * mm, v(25.5, 28.69) * mm, v(27.77, 28.85) * mm, v(29.6, 28.9) * mm, v(31, 28.93) * mm, v(32.38, 28.9) * mm, v(34.22, 28.85) * mm, v(36.5, 28.69) * mm, v(39.15, 28.38) * mm, v(41.73, 27.95) * mm, v(44.22, 27.4) * mm, v(46.59, 26.75) * mm, v(48.45, 26.11) * mm, v(49.87, 25.55) * mm, v(50.9, 25.1) * mm, v(51.88, 24.62) * mm, v(53.12, 23.95) * mm, v(54.54, 23.07) * mm, v(56.02, 21.92) * mm, v(57.27, 20.7) * mm, v(58.29, 19.39) * mm, v(59.04, 18) * mm, v(59.52, 16.54) * mm, v(59.62, 15.53) * mm, v(59.62, 15.02) * mm]});
            skLineSegment(sketch, "E103.5", {"start": v(18.11, 2.57) * mm, "end": v(24.71, 1.58) * mm});
            skLineSegment(sketch, "E103.6", {"start": v(43.87, 2.57) * mm, "end": v(37.27, 1.58) * mm});
            skArc(sketch, "E103.7", {"start": v(49.6, -23.08) * mm, "mid": v(67.67, -28.23) * mm, "end": v(49.6, -33.39) * mm});
            skArc(sketch, "E103.8", {"start": v(50.3, -24.28) * mm, "mid": v(66.47, -28.23) * mm, "end": v(50.3, -32.19) * mm});
            skLineSegment(sketch, "E104", {"start": v(-37.27, 1.58) * mm, "end": v(-24.71, 1.58) * mm});
            skLineSegment(sketch, "E105", {"start": v(-36.07, 2.54) * mm, "end": v(-25.91, 2.54) * mm});
            skLineSegment(sketch, "E106", {"start": v(25.91, 2.54) * mm, "end": v(36.07, 2.54) * mm});
            skLineSegment(sketch, "E107", {"start": v(37.27, 1.58) * mm, "end": v(24.71, 1.58) * mm});
            skArc(sketch, "E108", {"start": v(-49.6, -33.39) * mm, "mid": v(-48.34, -28.23) * mm, "end": v(-49.6, -23.08) * mm});
            skArc(sketch, "E109", {"start": v(-50.3, -32.19) * mm, "mid": v(-49.49, -28.23) * mm, "end": v(-50.3, -24.28) * mm});
            skArc(sketch, "E110", {"start": v(49.6, -23.08) * mm, "mid": v(48.13, -28.23) * mm, "end": v(49.6, -33.39) * mm});
            skArc(sketch, "E111", {"start": v(50.3, -24.28) * mm, "mid": v(49.33, -28.23) * mm, "end": v(50.3, -32.19) * mm});
            const initialGuessF6  = {"E102.0": [-0.030992886423162575, 0.015020336248152173, -1, 0, 0.02867695838303173, 0.013772825850373925, 1.7915767265639533, 1.3500159270258403], "E103.0": [-0.030992886423162575, 0.015020336248152173, -1, 0, 0.027432, 0.0127, 1.7570566303714537, 1.3845360232183401], "E103.3": [0.030992886423162575, 0.015020336248152173, 1, 0, 0.027432, 0.0127, 4.898649283961246, 4.526128676808133]};
            skSetInitialGuess(sketch, initialGuessF6);
            skSolve(sketch);
        }
        {
            var Q0;
            Q0=makeQuery(id+"F6.imprint","IMPRINT",FACE,{"disambiguationData":[TD([[makeQuery(id+"F6.imprint","IMPRINT",EDGE,{"derivedFrom":sQuery(id+"F6.wireOp",EDGE,"E103.3")}),-1.0]])]});
            var Q1;
            Q1=makeQuery(id+"F6.imprint","IMPRINT",FACE,{"disambiguationData":[TD([[makeQuery(id+"F6.imprint","IMPRINT",EDGE,{"derivedFrom":sQuery(id+"F6.wireOp",EDGE,"E103.7")}),-1.0]])]});
            var Q2;
            {var subQ1=sQuery(id+"F6.wireOp",EDGE,"E102.0");Q2=makeQuery(id+"F6.imprint","IMPRINT",FACE,{"disambiguationData":[TD([[makeQuery(id+"F6.imprint","IMPRINT",EDGE,{"derivedFrom":subQ1}),-1.0]])]});}
            var Q3;
            {var subQ5=sQuery(id+"F6.wireOp",EDGE,"E105");Q3=makeQuery(id+"F6.imprint","IMPRINT",FACE,{"disambiguationData":[TD([[makeQuery(id+"F6.imprint","IMPRINT",EDGE,{"derivedFrom":subQ5}),-1.0]])]});}
            var Q4;
            Q4=makeQuery(id+"F6.imprint","IMPRINT",FACE,{"disambiguationData":[TD([[makeQuery(id+"F6.imprint","IMPRINT",EDGE,{"derivedFrom":sQuery(id+"F6.wireOp",EDGE,"E103.1")}),1.0]])]});
            extrude(context, id + "F7", {"entities" : qUnion([Q0, Q1, Q2, Q3, Q4]), "operationType" : NewBodyOperationType.ADD, "depth" : 58.42 * mm, "offsetDistance" : 25.4 * mm, "hasSecondDirection" : true, "secondDirectionOppositeDirection" : true, "secondDirectionDepth" : 43.18 * mm});
        }
        {
            var Q0;
            Q0=makeQuery(id+"F7.opExtrude","CAP_FACE",FACE,{"disambiguationData":[OSD([sQuery(id+"F6.wireOp",EDGE,"E103.1"),sQuery(id+"F6.wireOp",EDGE,"E103.2"),sQuery(id+"F6.wireOp",EDGE,"E108"),sQuery(id+"F6.wireOp",EDGE,"E109")])],"isStart":false});
            var sketch = newSketch(context, id + "F8", { "sketchPlane" : qUnion([Q0])});
            skCircle(sketch, "E112.0", {"center": v(-59.58, -28.23) * mm, "radius": 11.24 * mm});
            skEllipticalArc(sketch, "E112.1", {});
            skLineSegment(sketch, "E112.2", {"start": v(-37.27, 1.58) * mm, "end": v(-24.71, 1.58) * mm});
            skFitSpline(sketch, "E112.3", {"points": [v(59.62, 15.02) * mm, v(59.62, 14.51) * mm, v(59.52, 13.5) * mm, v(59.04, 12.04) * mm, v(58.29, 10.65) * mm, v(57.27, 9.35) * mm, v(56.02, 8.12) * mm, v(54.54, 6.97) * mm, v(53.12, 6.09) * mm, v(51.88, 5.42) * mm, v(50.9, 4.95) * mm, v(49.87, 4.5) * mm, v(48.45, 3.93) * mm, v(46.59, 3.29) * mm, v(44.22, 2.63) * mm, v(41.73, 2.09) * mm, v(39.15, 1.66) * mm, v(36.5, 1.35) * mm, v(34.22, 1.2) * mm, v(32.38, 1.13) * mm, v(31, 1.12) * mm, v(29.6, 1.13) * mm, v(27.77, 1.2) * mm, v(25.5, 1.35) * mm, v(22.83, 1.66) * mm, v(20.25, 2.09) * mm, v(17.77, 2.63) * mm, v(15.4, 3.29) * mm, v(13.53, 3.93) * mm, v(12.11, 4.5) * mm, v(11.08, 4.95) * mm, v(10.1, 5.42) * mm, v(8.86, 6.09) * mm, v(7.45, 6.97) * mm, v(5.97, 8.12) * mm, v(4.71, 9.35) * mm, v(3.7, 10.65) * mm, v(2.94, 12.04) * mm, v(2.47, 13.5) * mm, v(2.3, 15.02) * mm, v(2.47, 16.54) * mm, v(2.94, 18) * mm, v(3.7, 19.39) * mm, v(4.71, 20.7) * mm, v(5.97, 21.92) * mm, v(7.45, 23.07) * mm, v(8.86, 23.95) * mm, v(10.1, 24.62) * mm, v(11.08, 25.1) * mm, v(12.11, 25.55) * mm, v(13.53, 26.11) * mm, v(15.4, 26.75) * mm, v(17.77, 27.4) * mm, v(20.25, 27.95) * mm, v(22.83, 28.38) * mm, v(25.5, 28.69) * mm, v(27.77, 28.85) * mm, v(29.6, 28.9) * mm, v(31, 28.93) * mm, v(32.38, 28.9) * mm, v(34.22, 28.85) * mm, v(36.5, 28.69) * mm, v(39.15, 28.38) * mm, v(41.73, 27.95) * mm, v(44.22, 27.4) * mm, v(46.59, 26.75) * mm, v(48.45, 26.11) * mm, v(49.87, 25.55) * mm, v(50.9, 25.1) * mm, v(51.88, 24.62) * mm, v(53.12, 23.95) * mm, v(54.54, 23.07) * mm, v(56.02, 21.92) * mm, v(57.27, 20.7) * mm, v(58.29, 19.39) * mm, v(59.04, 18) * mm, v(59.52, 16.54) * mm, v(59.62, 15.53) * mm, v(59.62, 15.02) * mm]});
            skLineSegment(sketch, "E112.4", {"start": v(43.87, 2.57) * mm, "end": v(37.27, 1.58) * mm});
            skLineSegment(sketch, "E112.5", {"start": v(37.27, 1.58) * mm, "end": v(24.71, 1.58) * mm});
            skLineSegment(sketch, "E112.6", {"start": v(18.11, 2.57) * mm, "end": v(24.71, 1.58) * mm});
            skCircle(sketch, "E112.7", {"center": v(57.9, -28.23) * mm, "radius": 9.77 * mm});
            skCircle(sketch, "E113", {"center": v(-31, 15.02) * mm, "radius": 5.02 * mm});
            skCircle(sketch, "E114", {"center": v(-13.4, 14.1) * mm, "radius": 3.89 * mm});
            skCircle(sketch, "E115", {"center": v(-47.7, 15.47) * mm, "radius": 4.42 * mm});
            skCircle(sketch, "E116", {"center": v(-58.9, -22.36) * mm, "radius": 1.44 * mm});
            skCircle(sketch, "E117", {"center": v(-59.58, -28.23) * mm, "radius": 1.74 * mm});
            skCircle(sketch, "E118", {"center": v(-56.6, -33.56) * mm, "radius": 1.4 * mm});
            skCircle(sketch, "E119", {"center": v(57.9, -28.23) * mm, "radius": 1.67 * mm});
            skCircle(sketch, "E120", {"center": v(59.63, -33.33) * mm, "radius": 1.29 * mm});
            skCircle(sketch, "E121", {"center": v(57.11, -23.28) * mm, "radius": 1.82 * mm});
            skCircle(sketch, "E122", {"center": v(16.88, 16.84) * mm, "radius": 3.68 * mm});
            skCircle(sketch, "E123", {"center": v(45.46, 17.07) * mm, "radius": 3.96 * mm});
            skCircle(sketch, "E124", {"center": v(31.28, 13.41) * mm, "radius": 3.7 * mm});
            const initialGuessF8  = {"E112.1": [-0.030992886423162575, 0.015020336248152173, -1, 0, 0.02867695838303173, 0.013772825850373925, 1.7915767265639533, 1.3500159270258403]};
            skSetInitialGuess(sketch, initialGuessF8);
            skSolve(sketch);
        }
        {
            var Q0;
            Q0=makeQuery(id+"F8.imprint","IMPRINT",FACE,{"disambiguationData":[TD([[makeQuery(id+"F8.imprint","IMPRINT",EDGE,{"derivedFrom":sQuery(id+"F8.wireOp",EDGE,"E112.1")}),1.0]])]});
            var Q1;
            Q1=makeQuery(id+"F8.imprint","IMPRINT",FACE,{"disambiguationData":[TD([[makeQuery(id+"F8.imprint","IMPRINT",EDGE,{"derivedFrom":sQuery(id+"F8.wireOp",EDGE,"E116")}),-1.0]])]});
            var Q2;
            Q2=makeQuery(id+"F8.imprint","IMPRINT",FACE,{"disambiguationData":[TD([[makeQuery(id+"F8.imprint","IMPRINT",EDGE,{"derivedFrom":sQuery(id+"F8.wireOp",EDGE,"E112.3")}),-1.0]])]});
            var Q3;
            Q3=makeQuery(id+"F8.imprint","IMPRINT",FACE,{"disambiguationData":[TD([[makeQuery(id+"F8.imprint","IMPRINT",EDGE,{"derivedFrom":sQuery(id+"F8.wireOp",EDGE,"E112.7")}),1.0]])]});
            extrude(context, id + "F9", {"entities" : qUnion([Q0, Q1, Q2, Q3]), "operationType" : NewBodyOperationType.ADD, "oppositeDirection" : true, "depth" : 2.03 * mm, "offsetDistance" : 25.4 * mm});
        }
        {
            var Q0;
            Q0=qCreatedBy(makeId("Top.planeOp"),FACE);
            var sketch = newSketch(context, id + "F10", { "sketchPlane" : qUnion([Q0])});
            skLineSegment(sketch, "E125", {"start": v(22.71, 0) * mm, "end": v(17.71, 2.89) * mm});
            skLineSegment(sketch, "E126", {"start": v(17.71, 2.89) * mm, "end": v(17.71, 8.58) * mm});
            skLineSegment(sketch, "E127", {"start": v(17.71, 8.58) * mm, "end": v(44.27, 8.58) * mm});
            skLineSegment(sketch, "E128", {"start": v(44.27, 8.58) * mm, "end": v(44.27, 2.89) * mm});
            skLineSegment(sketch, "E129", {"start": v(44.27, 2.89) * mm, "end": v(39.27, 0) * mm});
            skLineSegment(sketch, "E130", {"start": v(22.71, 0) * mm, "end": v(22.71, -1.2) * mm});
            skLineSegment(sketch, "E131", {"start": v(39.27, 0) * mm, "end": v(39.27, -1.2) * mm});
            skFitSpline(sketch, "E132", {"points": [v(22.71, -1.2) * mm, v(4.61, -11.08) * mm, v(4.61, -15.08) * mm, v(36.3, -31.2) * mm, v(70.61, -15.08) * mm, v(70.61, -11.08) * mm, v(39.27, -1.2) * mm], "startDerivative": vector(-127.2, -72.78) * mm, "endDerivative": vector(-183.4, 56.54) * mm});
            skFitSpline(sketch, "E133.0", {"points": [v(23.3, -2.24) * mm, v(21.96, -3.01) * mm, v(19.22, -4.47) * mm, v(15.17, -6.45) * mm, v(12.07, -7.94) * mm, v(9.88, -9.05) * mm, v(8.4, -9.84) * mm, v(7.15, -10.6) * mm, v(6.14, -11.3) * mm, v(5.43, -11.92) * mm, v(5.12, -12.33) * mm, v(5, -12.58) * mm, v(4.97, -12.73) * mm, v(4.95, -12.89) * mm, v(4.98, -13.15) * mm, v(5.14, -13.65) * mm, v(5.65, -14.5) * mm, v(6.48, -15.6) * mm, v(7.6, -16.82) * mm, v(8.98, -18.16) * mm, v(11.15, -20.03) * mm, v(14.4, -22.46) * mm, v(19, -25.22) * mm, v(24.15, -27.6) * mm, v(28.75, -29.04) * mm, v(32.53, -29.74) * mm, v(35.4, -30.02) * mm, v(38.27, -30.01) * mm, v(41.17, -29.73) * mm, v(44.06, -29.2) * mm, v(47.87, -28.21) * mm, v(52.5, -26.5) * mm, v(57.64, -23.95) * mm, v(62.19, -21.11) * mm, v(65.32, -18.73) * mm, v(67.33, -16.94) * mm, v(68.57, -15.7) * mm, v(69.5, -14.59) * mm, v(70.01, -13.83) * mm, v(70.24, -13.36) * mm, v(70.33, -13.08) * mm, v(70.37, -12.87) * mm, v(70.36, -12.73) * mm, v(70.33, -12.6) * mm, v(70.27, -12.46) * mm, v(70.13, -12.27) * mm, v(69.83, -11.97) * mm, v(69.2, -11.5) * mm, v(68.07, -10.9) * mm, v(66.63, -10.28) * mm, v(64.9, -9.64) * mm, v(62.93, -9) * mm, v(60.02, -8.14) * mm, v(55.91, -7.02) * mm, v(50.47, -5.6) * mm, v(44.73, -4.06) * mm, v(40.84, -2.94) * mm, v(38.92, -2.35) * mm]});
            skLineSegment(sketch, "E134", {"start": v(23.3, -2.24) * mm, "end": v(38.92, -2.35) * mm});
            skLineSegment(sketch, "E135", {"start": v(22.71, -1.2) * mm, "end": v(23.74, -0.76) * mm});
            skLineSegment(sketch, "E136", {"start": v(23.74, -0.76) * mm, "end": v(38.44, -0.86) * mm});
            skLineSegment(sketch, "E137", {"start": v(38.44, -0.86) * mm, "end": v(39.27, -1.2) * mm});
            skSolve(sketch);
        }
        {
            var Q0;
            Q0=makeQuery(id+"F10.imprint","IMPRINT",FACE,{"disambiguationData":[TD([[makeQuery(id+"F10.imprint","IMPRINT",EDGE,{"derivedFrom":sQuery(id+"F10.wireOp",EDGE,"E132")}),1.0]])]});
            var Q1;
            Q1=makeQuery(id+"F7.opExtrude","CAP_FACE",FACE,{"disambiguationData":[OSD([sQuery(id+"F6.wireOp",EDGE,"E102.0"),sQuery(id+"F6.wireOp",EDGE,"E103.0"),sQuery(id+"F6.wireOp",EDGE,"E104"),sQuery(id+"F6.wireOp",EDGE,"E105")])],"isStart":true});
            var Q2;
            Q2=makeQuery(id+"F9.boolean.opBoolean","MERGE",FACE,{"derivedFrom":[makeQuery(id+"F7.opExtrude","CAP_FACE",FACE,{"disambiguationData":[OSD([sQuery(id+"F6.wireOp",EDGE,"E102.0"),sQuery(id+"F6.wireOp",EDGE,"E103.0"),sQuery(id+"F6.wireOp",EDGE,"E104"),sQuery(id+"F6.wireOp",EDGE,"E105")])],"isStart":false}),makeQuery(id+"F9.opExtrude","CAP_FACE",FACE,{"disambiguationData":[OSD([sQuery(id+"F8.wireOp",EDGE,"E112.1"),sQuery(id+"F8.wireOp",EDGE,"E112.2"),sQuery(id+"F8.wireOp",EDGE,"E113"),sQuery(id+"F8.wireOp",EDGE,"E114"),sQuery(id+"F8.wireOp",EDGE,"E115")])],"isStart":true})]});
            extrude(context, id + "F11", {"entities" : qUnion([Q0]), "endBound" : BoundingType.UP_TO_SURFACE, "depth" : 25 * mm, "endBoundEntityFace" : qUnion([Q1]), "offsetDistance" : 25 * mm, "hasSecondDirection" : true, "secondDirectionBound" : SecondDirectionBoundingType.UP_TO_SURFACE, "secondDirectionOppositeDirection" : true, "secondDirectionDepth" : 25 * mm, "secondDirectionBoundEntityFace" : qUnion([Q2])});
        }
        {
            var Q0;
            Q0=makeQuery(id+"F10.imprint","IMPRINT",FACE,{"disambiguationData":[TD([[makeQuery(id+"F10.imprint","IMPRINT",EDGE,{"derivedFrom":sQuery(id+"F10.wireOp",EDGE,"E125")}),-1.0]])]});
            var Q1;
            Q1=makeQuery(id+"F5.opExtrude","CAP_FACE",FACE,{"disambiguationData":[OSD([sQuery(id+"F3.wireOp",EDGE,"E80.MirrorCS"),sQuery(id+"F3.wireOp",EDGE,"E83.MirrorCS"),sQuery(id+"F3.wireOp",EDGE,"E86.MirrorCS"),sQuery(id+"F3.wireOp",EDGE,"E88.MirrorCS"),sQuery(id+"F3.wireOp",EDGE,"E89.MirrorCS"),sQuery(id+"F3.wireOp",EDGE,"E90.MirrorCS"),sQuery(id+"F3.wireOp",EDGE,"E91.MirrorCS"),sQuery(id+"F3.wireOp",EDGE,"E92.MirrorCS"),sQuery(id+"F3.wireOp",EDGE,"E93.MirrorCS"),sQuery(id+"F3.wireOp",EDGE,"E94.MirrorCS"),sQuery(id+"F3.wireOp",EDGE,"E98.MirrorCS"),sQuery(id+"F3.wireOp",EDGE,"E100")])],"isStart":true});
            extrude(context, id + "F12", {"entities" : qUnion([Q0]), "operationType" : NewBodyOperationType.ADD, "endBound" : BoundingType.UP_TO_SURFACE, "depth" : 25 * mm, "endBoundEntityFace" : qUnion([Q1]), "offsetDistance" : 25 * mm});
        }
        {
            var Q0;
            Q0=makeQuery(id+"F10.imprint","IMPRINT",FACE,{"disambiguationData":[TD([[makeQuery(id+"F10.imprint","IMPRINT",EDGE,{"derivedFrom":sQuery(id+"F10.wireOp",EDGE,"E133.0")}),1.0]])]});
            var Q1;
            Q1=makeQuery(id+"F11.opExtrude","CAP_FACE",FACE,{"disambiguationData":[OSD([sQuery(id+"F10.wireOp",EDGE,"E132"),sQuery(id+"F10.wireOp",EDGE,"E133.0"),sQuery(id+"F10.wireOp",EDGE,"E134"),sQuery(id+"F10.wireOp",EDGE,"E135"),sQuery(id+"F10.wireOp",EDGE,"E136"),sQuery(id+"F10.wireOp",EDGE,"E137")])],"isStart":true});
            var Q2;
            Q2=makeQuery(id+"F9.opExtrude","CAP_FACE",FACE,{"disambiguationData":[OSD([sQuery(id+"F8.wireOp",EDGE,"E112.1"),sQuery(id+"F8.wireOp",EDGE,"E112.2"),sQuery(id+"F8.wireOp",EDGE,"E113"),sQuery(id+"F8.wireOp",EDGE,"E114"),sQuery(id+"F8.wireOp",EDGE,"E115")])],"isStart":false});
            extrude(context, id + "F13", {"entities" : qUnion([Q0]), "operationType" : NewBodyOperationType.ADD, "endBound" : BoundingType.UP_TO_SURFACE, "oppositeDirection" : true, "depth" : 58.5 * mm, "endBoundEntityFace" : qUnion([Q1]), "offsetDistance" : 25 * mm});
        }
        {
            var Q0;
            Q0=makeQuery(id+"F10.imprint","IMPRINT",FACE,{"disambiguationData":[TD([[makeQuery(id+"F10.imprint","IMPRINT",EDGE,{"derivedFrom":sQuery(id+"F10.wireOp",EDGE,"E133.0")}),1.0]])]});
            var Q1;
            Q1=makeQuery(id+"F9.opExtrude","CAP_FACE",FACE,{"disambiguationData":[OSD([sQuery(id+"F8.wireOp",EDGE,"E112.1"),sQuery(id+"F8.wireOp",EDGE,"E112.2"),sQuery(id+"F8.wireOp",EDGE,"E113"),sQuery(id+"F8.wireOp",EDGE,"E114"),sQuery(id+"F8.wireOp",EDGE,"E115")])],"isStart":false});
            extrude(context, id + "F14", {"entities" : qUnion([Q0]), "operationType" : NewBodyOperationType.REMOVE, "endBound" : BoundingType.UP_TO_SURFACE, "oppositeDirection" : true, "depth" : 25 * mm, "endBoundEntityFace" : qUnion([Q1]), "offsetDistance" : 25 * mm});
        }
        {
            var Q0;
            Q0=makeQuery(id+"F14.boolean.opBoolean","COPY",FACE,{"derivedFrom":makeQuery(id+"F14.opExtrude","CAP_FACE",FACE,{"disambiguationData":[OSD([sQuery(id+"F10.wireOp",EDGE,"E133.0"),sQuery(id+"F10.wireOp",EDGE,"E134")])],"isStart":false})});
            var sketch = newSketch(context, id + "F15", { "sketchPlane" : qUnion([Q0])});
            skArc(sketch, "E138", {"start": v(32.5, -7.3) * mm, "mid": v(29.43, -12.05) * mm, "end": v(33.65, -15.81) * mm});
            skArc(sketch, "E139", {"start": v(32.69, -7.96) * mm, "mid": v(30.15, -12.2) * mm, "end": v(34.15, -15.1) * mm});
            skArc(sketch, "E140", {"start": v(32.69, -7.96) * mm, "mid": v(32.92, -7.53) * mm, "end": v(32.5, -7.3) * mm});
            skArc(sketch, "E141.1.0", {"start": v(28.27, -10.89) * mm, "mid": v(28.71, -15.81) * mm, "end": v(33.65, -15.81) * mm});
            skArc(sketch, "E141.1.1", {"start": v(27.72, -10.47) * mm, "mid": v(28.04, -16.12) * mm, "end": v(33.67, -16.68) * mm});
            skArc(sketch, "E141.1.2", {"start": v(28.27, -10.89) * mm, "mid": v(28.2, -10.4) * mm, "end": v(27.72, -10.47) * mm});
            skArc(sketch, "E141.2.0", {"start": v(26.42, -15.86) * mm, "mid": v(29.67, -19.58) * mm, "end": v(33.67, -16.68) * mm});
            skArc(sketch, "E141.2.1", {"start": v(25.73, -15.84) * mm, "mid": v(29.3, -20.22) * mm, "end": v(34.19, -17.37) * mm});
            skArc(sketch, "E141.2.2", {"start": v(26.42, -15.86) * mm, "mid": v(26.08, -15.5) * mm, "end": v(25.73, -15.84) * mm});
            skArc(sketch, "E141.3.0", {"start": v(27.84, -20.97) * mm, "mid": v(32.66, -22.07) * mm, "end": v(34.19, -17.37) * mm});
            skArc(sketch, "E141.3.1", {"start": v(27.28, -21.36) * mm, "mid": v(32.74, -22.8) * mm, "end": v(35.01, -17.62) * mm});
            skArc(sketch, "E141.3.2", {"start": v(27.84, -20.97) * mm, "mid": v(27.36, -20.88) * mm, "end": v(27.28, -21.36) * mm});
            skArc(sketch, "E141.4.0", {"start": v(32, -24.27) * mm, "mid": v(36.54, -22.32) * mm, "end": v(35.01, -17.62) * mm});
            skArc(sketch, "E141.4.1", {"start": v(31.77, -24.91) * mm, "mid": v(37.04, -22.86) * mm, "end": v(35.83, -17.34) * mm});
            skArc(sketch, "E141.4.2", {"start": v(32, -24.27) * mm, "mid": v(31.56, -24.48) * mm, "end": v(31.77, -24.91) * mm});
            skArc(sketch, "E141.5.0", {"start": v(37.3, -24.49) * mm, "mid": v(39.83, -20.25) * mm, "end": v(35.83, -17.34) * mm});
            skArc(sketch, "E141.5.1", {"start": v(37.5, -25.15) * mm, "mid": v(40.55, -20.4) * mm, "end": v(36.33, -16.63) * mm});
            skArc(sketch, "E141.5.2", {"start": v(37.3, -24.49) * mm, "mid": v(37.07, -24.92) * mm, "end": v(37.5, -25.15) * mm});
            skArc(sketch, "E141.6.0", {"start": v(41.72, -21.56) * mm, "mid": v(41.27, -16.63) * mm, "end": v(36.33, -16.63) * mm});
            skArc(sketch, "E141.6.1", {"start": v(42.26, -21.97) * mm, "mid": v(41.94, -16.33) * mm, "end": v(36.32, -15.77) * mm});
            skArc(sketch, "E141.6.2", {"start": v(41.72, -21.56) * mm, "mid": v(41.78, -22.04) * mm, "end": v(42.26, -21.97) * mm});
            skArc(sketch, "E141.7.0", {"start": v(43.57, -16.59) * mm, "mid": v(40.31, -12.86) * mm, "end": v(36.32, -15.77) * mm});
            skArc(sketch, "E141.7.1", {"start": v(44.25, -16.6) * mm, "mid": v(40.68, -12.22) * mm, "end": v(35.8, -15.08) * mm});
            skArc(sketch, "E141.7.2", {"start": v(43.57, -16.59) * mm, "mid": v(43.9, -16.94) * mm, "end": v(44.25, -16.6) * mm});
            skArc(sketch, "E141.8.0", {"start": v(42.14, -11.48) * mm, "mid": v(37.32, -10.38) * mm, "end": v(35.8, -15.08) * mm});
            skArc(sketch, "E141.8.1", {"start": v(42.7, -11.09) * mm, "mid": v(37.24, -9.65) * mm, "end": v(34.97, -14.82) * mm});
            skArc(sketch, "E141.8.2", {"start": v(42.14, -11.48) * mm, "mid": v(42.62, -11.56) * mm, "end": v(42.7, -11.09) * mm});
            skArc(sketch, "E141.9.0", {"start": v(37.99, -8.18) * mm, "mid": v(33.44, -10.12) * mm, "end": v(34.97, -14.82) * mm});
            skArc(sketch, "E141.9.1", {"start": v(38.21, -7.53) * mm, "mid": v(32.95, -9.58) * mm, "end": v(34.15, -15.1) * mm});
            skArc(sketch, "E141.9.2", {"start": v(37.99, -8.18) * mm, "mid": v(38.42, -7.97) * mm, "end": v(38.21, -7.53) * mm});
            skPoint(sketch, "E141.center", {"position": v(35, -16.22) * mm});
            skPoint(sketch, "E142.orphan", {"position": v(34.03, -15.41) * mm});
            skPoint(sketch, "E143.orphan", {"position": v(33.74, -16.13) * mm});
            skPoint(sketch, "E144.orphan", {"position": v(34.69, -15) * mm});
            skPoint(sketch, "E145.orphan", {"position": v(35.47, -15.06) * mm});
            skPoint(sketch, "E146.orphan", {"position": v(36.06, -15.56) * mm});
            skPoint(sketch, "E147.orphan", {"position": v(36.25, -16.31) * mm});
            skPoint(sketch, "E148.orphan", {"position": v(35.95, -17.03) * mm});
            skPoint(sketch, "E149.orphan", {"position": v(35.3, -17.44) * mm});
            skPoint(sketch, "E150.orphan", {"position": v(34.52, -17.39) * mm});
            skPoint(sketch, "E151.orphan", {"position": v(33.92, -16.89) * mm});
            skPoint(sketch, "E152.end.orphan", {"position": v(35, -15.63) * mm});
            skSolve(sketch);
        }
        {
            var Q0;
            Q0 = qSketchRegion(id + "F15", true);
            extrude(context, id + "F16", {"entities" : qUnion([Q0]), "operationType" : NewBodyOperationType.REMOVE, "oppositeDirection" : true, "depth" : 25 * mm, "offsetDistance" : 25 * mm});
        }
    });
